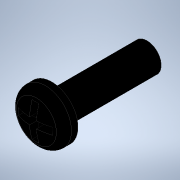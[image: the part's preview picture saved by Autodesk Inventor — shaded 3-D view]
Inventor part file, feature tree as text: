
AUTODESK INVENTOR PART (.ipt)
format: ipt  version: 2022 (Build 260153000, 153)  size: 152,576 bytes
history: native  units: mm
features: other x2, extrude x1, sketch x1
ambient origin geometry x8: Origin, YZ Plane, XZ Plane, XY Plane, X Axis, Y Axis, Z Axis, Center Point
bodies: Body1 (feature_tree)
feature tree (4):
  other  "ソリッド1"
  parser-record x1  (decoder bookkeeping rows leaked as tree rows — omitted from the tree; the rows remain in map.json)
  extrude  "押し出し1"  Depth=1.0mm TaperAngle=0.0deg
  sketch  "スケッチ1"
